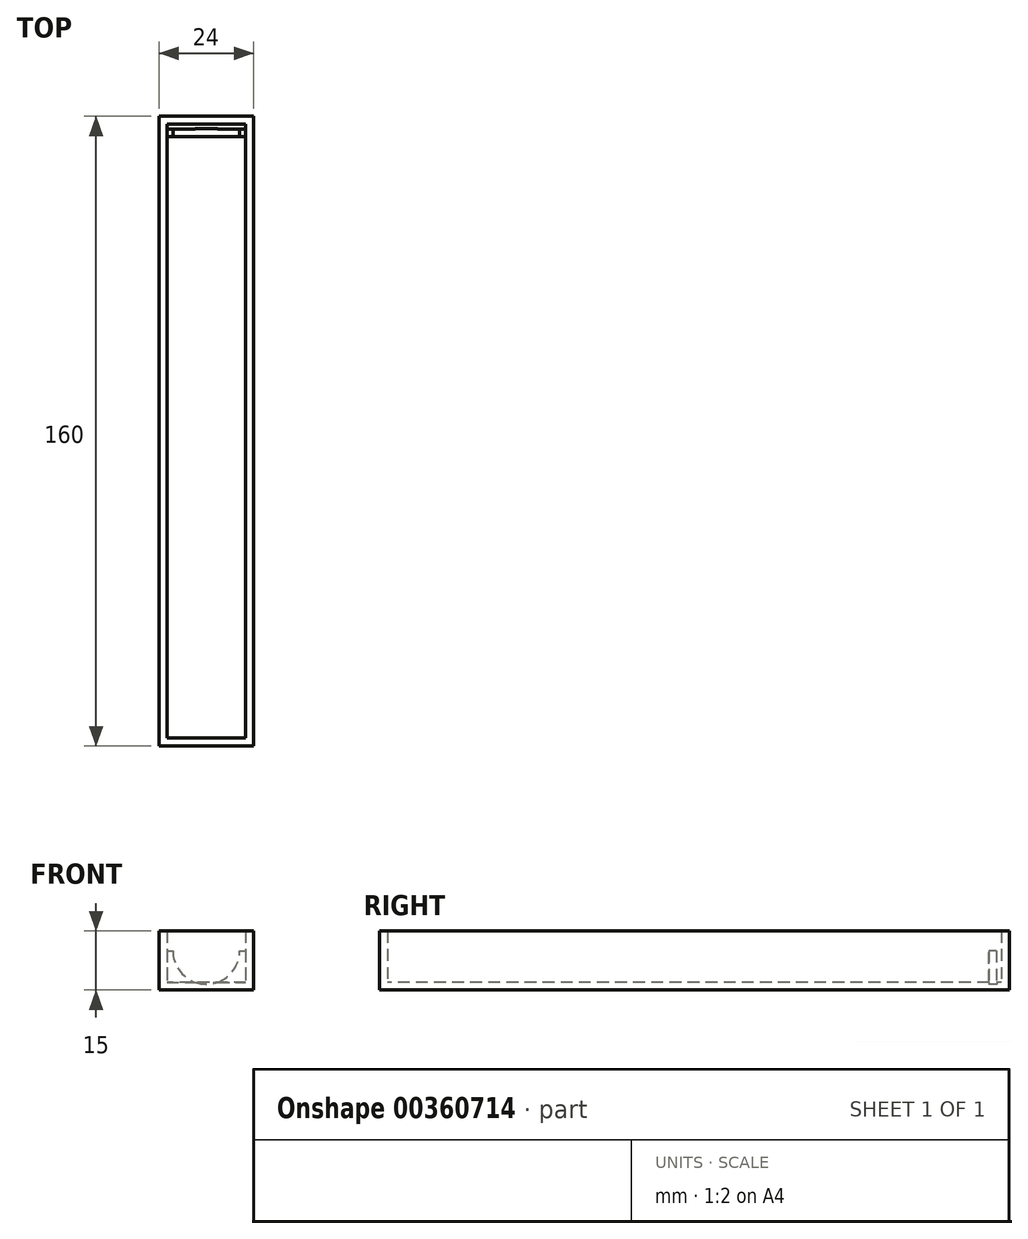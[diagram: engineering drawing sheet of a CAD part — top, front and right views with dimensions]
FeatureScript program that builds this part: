
annotation { "Feature Type Name" : "Feature", "Feature Type Description" : "" }
export const myFeature = defineFeature(function(context is Context, id is Id, definition is map)
    precondition{}
    {
        {
            var Q0;
            Q0=qCreatedBy(makeId("Top.planeOp"),FACE);
            var sketch = newSketch(context, id + "F0", { "sketchPlane" : qUnion([Q0])});
            skLineSegment(sketch, "E0", {"start": v(0, 210.08) * mm, "end": v(0, -222.44) * mm, "construction": true});
            skLineSegment(sketch, "E1", {"start": v(189.92, 0) * mm, "end": v(-229.6, 0) * mm, "construction": true});
            skLineSegment(sketch, "E2.bottom", {"start": v(12, 80) * mm, "end": v(-12, 80) * mm});
            skLineSegment(sketch, "E2.top", {"start": v(12, -80) * mm, "end": v(-12, -80) * mm});
            skLineSegment(sketch, "E2.left", {"start": v(12, 80) * mm, "end": v(12, -80) * mm});
            skLineSegment(sketch, "E2.right", {"start": v(-12, 80) * mm, "end": v(-12, -80) * mm});
            skPoint(sketch, "E2.middle", {"position": v(0, 0) * mm});
            skSolve(sketch);
        }
        {
            var Q0;
            Q0 = qSketchRegion(id + "F0", true);
            extrude(context, id + "F1", {"entities" : qUnion([Q0]), "depth" : 15 * mm});
        }
        {
            var Q0;
            Q0=makeQuery(id+"F1.opExtrude","CAP_FACE",FACE,{"disambiguationData":[OSD([sQuery(id+"F0.wireOp",EDGE,"E2.bottom"),sQuery(id+"F0.wireOp",EDGE,"E2.top"),sQuery(id+"F0.wireOp",EDGE,"E2.left"),sQuery(id+"F0.wireOp",EDGE,"E2.right")])],"isStart":false});
            shell(context, id + "F2", {"entities" : qUnion([Q0]), "thickness" : 2 * mm});
        }
        {
            var Q0;
            Q0=makeQuery(id+"F2.opShell","OFFSET_FACE",FACE,{"disambiguationData":[OSD([sQuery(id+"F0.wireOp",EDGE,"E2.bottom"),sQuery(id+"F0.wireOp",EDGE,"E2.top"),sQuery(id+"F0.wireOp",EDGE,"E2.left"),sQuery(id+"F0.wireOp",EDGE,"E2.right")])]});
            var sketch = newSketch(context, id + "F3", { "sketchPlane" : qUnion([Q0])});
            skLineSegment(sketch, "E3", {"start": v(-10, 76.76) * mm, "end": v(10, 76.76) * mm});
            skLineSegment(sketch, "E4", {"start": v(10, 76.76) * mm, "end": v(10, 74.86) * mm});
            skLineSegment(sketch, "E5", {"start": v(10, 74.86) * mm, "end": v(-10, 74.86) * mm});
            skLineSegment(sketch, "E6", {"start": v(-10, 74.86) * mm, "end": v(-10, 76.76) * mm});
            skSolve(sketch);
        }
        {
            var Q0;
            Q0 = qSketchRegion(id + "F3", true);
            extrude(context, id + "F4", {"entities" : qUnion([Q0]), "operationType" : NewBodyOperationType.ADD, "depth" : 8 * mm});
        }
        {
            var Q0;
            Q0=makeQuery(id+"F4.opExtrude","SWEPT_FACE",FACE,{"disambiguationData":[OSD([sQuery(id+"F3.wireOp",EDGE,"E5")])]});
            var sketch = newSketch(context, id + "F5", { "sketchPlane" : qUnion([Q0])});
            skCircle(sketch, "E7", {"center": v(0, 10) * mm, "radius": 8.5 * mm});
            skSolve(sketch);
        }
        {
            var Q0;
            Q0 = qSketchRegion(id + "F5", true);
            extrude(context, id + "F6", {"entities" : qUnion([Q0]), "operationType" : NewBodyOperationType.REMOVE, "oppositeDirection" : true, "depth" : 2 * mm});
        }
    });
